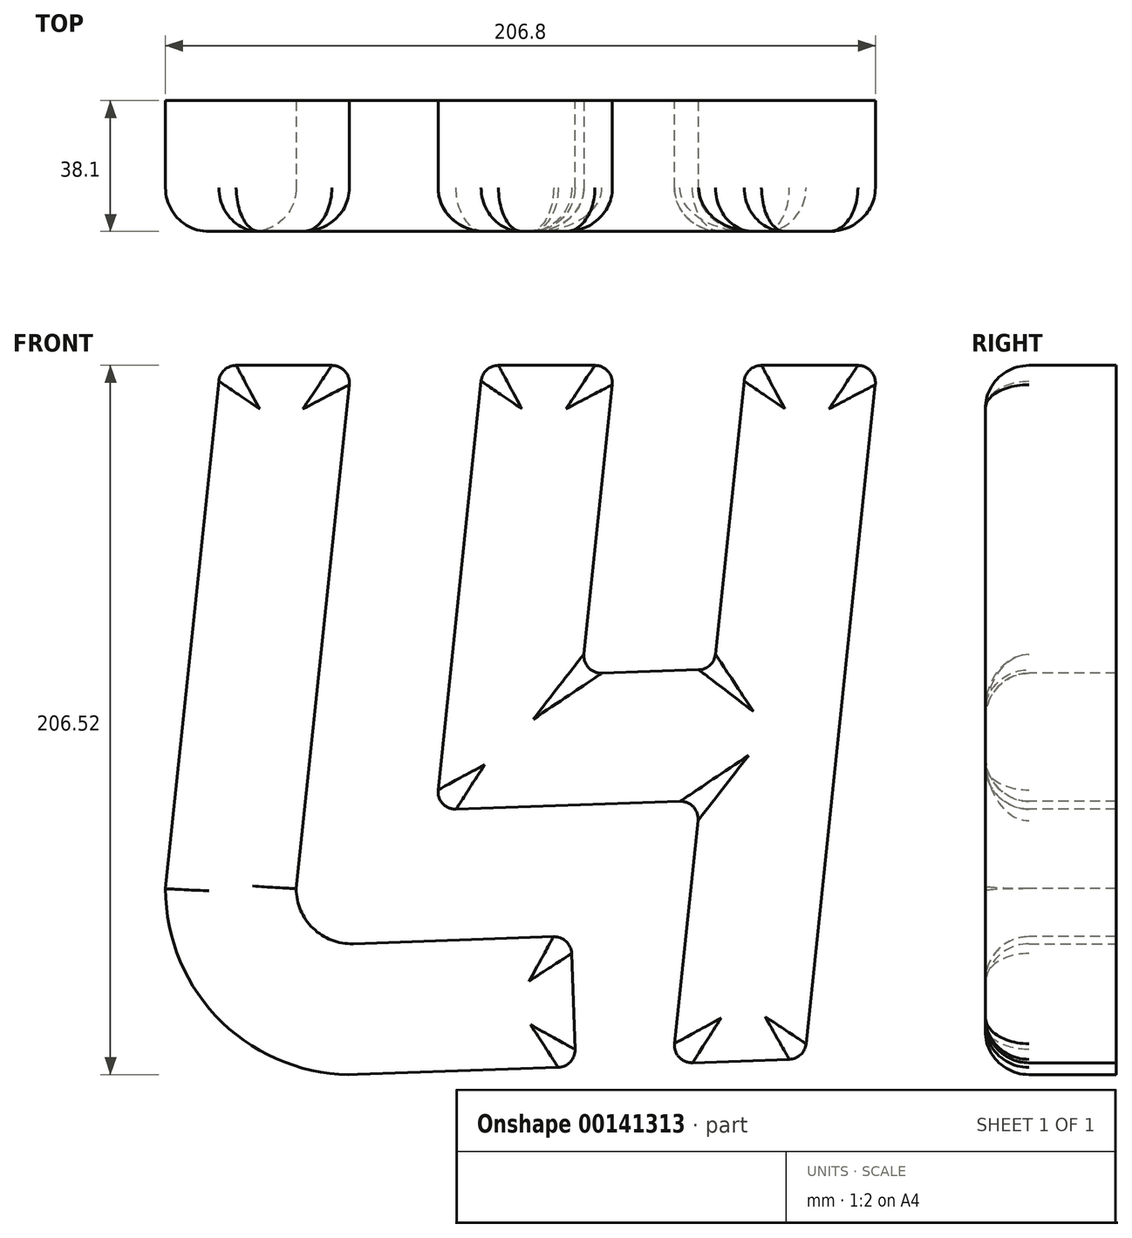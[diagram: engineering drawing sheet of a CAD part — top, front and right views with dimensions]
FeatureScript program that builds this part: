
annotation { "Feature Type Name" : "Feature", "Feature Type Description" : "" }
export const myFeature = defineFeature(function(context is Context, id is Id, definition is map)
    precondition{}
    {
        {
            var Q0;
            Q0=qCreatedBy(makeId("Top.planeOp"),FACE);
            cPlane(context, id + "F0", {"entities" : qUnion([Q0]), "cplaneType" : CPlaneType.OFFSET, "offset" : 76.2 * mm, "width" : 152.4 * mm, "height" : 152.4 * mm});
        }
        {
            var Q0;
            Q0=qCreatedBy(id+"F0.planeOp",FACE);
            var sketch = newSketch(context, id + "F1", { "sketchPlane" : qUnion([Q0])});
            skLineSegment(sketch, "E0.bottom", {"start": v(-19.05, 19.05) * mm, "end": v(19.05, 19.05) * mm});
            skLineSegment(sketch, "E0.top", {"start": v(-19.05, -19.05) * mm, "end": v(19.05, -19.05) * mm});
            skLineSegment(sketch, "E0.left", {"start": v(-19.05, 19.05) * mm, "end": v(-19.05, -19.05) * mm});
            skLineSegment(sketch, "E0.right", {"start": v(19.05, 19.05) * mm, "end": v(19.05, -19.05) * mm});
            skPoint(sketch, "E0.middle", {"position": v(0, 0) * mm});
            skSolve(sketch);
        }
        {
            var Q0;
            Q0=qCreatedBy(makeId("Front.planeOp"),FACE);
            var sketch = newSketch(context, id + "F2", { "sketchPlane" : qUnion([Q0])});
            skLineSegment(sketch, "E1", {"start": v(0, 0) * mm, "end": v(0, 76.2) * mm});
            skLineSegment(sketch, "E2", {"start": v(0, 0) * mm, "end": v(0, -76.2) * mm});
            skLineSegment(sketch, "E3", {"start": v(0, 76.2) * mm, "end": v(-16.02, -76.2) * mm});
            skSolve(sketch);
        }
        {
            var Q0;
            Q0=qCreatedBy(makeId("Top.planeOp"),FACE);
            cPlane(context, id + "F3", {"entities" : qUnion([Q0]), "cplaneType" : CPlaneType.OFFSET, "offset" : 76.2 * mm, "oppositeDirection" : true, "width" : 152.4 * mm, "height" : 152.4 * mm});
        }
        {
            var Q0;
            Q0=makeQuery(id+"F1.imprint","IMPRINT",FACE,{"disambiguationData":[TD([[makeQuery(id+"F1.imprint","IMPRINT",EDGE,{"derivedFrom":sQuery(id+"F1.wireOp",EDGE,"E0.bottom")}),-1.0]])]});
            var Q1;
            Q1=sQuery(id+"F2.wireOp",EDGE,"E3");
            sweep(context, id + "F4", {"profiles" : qUnion([Q0]), "path" : qUnion([Q1])});
        }
        {
            var Q0;
            Q0=qCreatedBy(id+"F3.planeOp",FACE);
            var sketch = newSketch(context, id + "F5", { "sketchPlane" : qUnion([Q0])});
            skLineSegment(sketch, "E4.0.0", {"start": v(3.03, -19.05) * mm, "end": v(3.03, 19.05) * mm});
            skLineSegment(sketch, "E4.0.1", {"start": v(3.03, 19.05) * mm, "end": v(19.05, 19.05) * mm});
            skLineSegment(sketch, "E4.0.2", {"start": v(19.05, 19.05) * mm, "end": v(19.05, -19.05) * mm});
            skLineSegment(sketch, "E4.0.3", {"start": v(19.05, -19.05) * mm, "end": v(3.03, -19.05) * mm});
            skSolve(sketch);
        }
        {
            var Q0;
            Q0=makeQuery(id+"F4.opSweep","CAP_FACE",FACE,{"disambiguationData":[OSD([sQuery(id+"F1.wireOp",EDGE,"E0.bottom"),sQuery(id+"F1.wireOp",EDGE,"E0.top"),sQuery(id+"F1.wireOp",EDGE,"E0.left"),sQuery(id+"F1.wireOp",EDGE,"E0.right"),sQuery(id+"F2.wireOp",VERTEX,"E3.end")])],"isStart":false});
            var Q1;
            Q1=sQuery(id+"F5.wireOp",EDGE,"E4.0.2");
            revolve(context, id + "F6", {"operationType" : NewBodyOperationType.ADD, "entities" : qUnion([Q0]), "axis" : qUnion([Q1]), "revolveType" : RevolveType.ONE_DIRECTION, "angle" : 92 * degree});
        }
        {
            var Q0;
            Q0=makeQuery(id+"F6.opRevolve","CAP_FACE",FACE,{"disambiguationData":[OSD([sQuery(id+"F1.wireOp",EDGE,"E0.bottom"),sQuery(id+"F1.wireOp",EDGE,"E0.top"),sQuery(id+"F1.wireOp",EDGE,"E0.left"),sQuery(id+"F1.wireOp",EDGE,"E0.right"),sQuery(id+"F2.wireOp",VERTEX,"E3.end")])],"isStart":false});
            extrude(context, id + "F7", {"entities" : qUnion([Q0]), "operationType" : NewBodyOperationType.ADD, "depth" : 63.5 * mm});
        }
        {
            var Q0;
            Q0=qCreatedBy(makeId("Front.planeOp"),FACE);
            cPlane(context, id + "F8", {"entities" : qUnion([Q0]), "cplaneType" : CPlaneType.OFFSET, "offset" : 19.05 * mm, "oppositeDirection" : true, "width" : 152.4 * mm, "height" : 152.4 * mm});
        }
        {
            var Q0;
            Q0=qCreatedBy(id+"F8.planeOp",FACE);
            var sketch = newSketch(context, id + "F9", { "sketchPlane" : qUnion([Q0])});
            skLineSegment(sketch, "E5.0.0", {"start": v(-19.05, 76.2) * mm, "end": v(-35.07, -76.2) * mm});
            skArc(sketch, "E5.0.1", {"start": v(-35.07, -76.2) * mm, "mid": v(-18.54, -115.13) * mm, "end": v(20.94, -130.28) * mm});
            skLineSegment(sketch, "E5.0.2", {"start": v(20.94, -130.28) * mm, "end": v(84.4, -128.07) * mm});
            skLineSegment(sketch, "E5.0.3", {"start": v(83.07, -90) * mm, "end": v(84.4, -128.07) * mm});
            skLineSegment(sketch, "E5.0.4", {"start": v(83.07, -90) * mm, "end": v(19.6, -92.2) * mm});
            skArc(sketch, "E5.0.5", {"start": v(19.6, -92.2) * mm, "mid": v(7.92, -87.72) * mm, "end": v(3.03, -76.2) * mm});
            skLineSegment(sketch, "E5.0.6", {"start": v(3.03, -76.2) * mm, "end": v(19.05, 76.2) * mm});
            skLineSegment(sketch, "E5.0.7", {"start": v(19.05, 76.2) * mm, "end": v(-19.05, 76.2) * mm});
            skLineSegment(sketch, "E6", {"start": v(14, 28.06) * mm, "end": v(51.88, 24.08) * mm, "construction": true});
            skLineSegment(sketch, "E7", {"start": v(72.28, -90.37) * mm, "end": v(70.95, -52.3) * mm, "construction": true});
            skLineSegment(sketch, "E8", {"start": v(51.88, 24.08) * mm, "end": v(57.36, 76.2) * mm});
            skLineSegment(sketch, "E9", {"start": v(51.88, 24.08) * mm, "end": v(43.75, -53.24) * mm});
            skLineSegment(sketch, "E10", {"start": v(43.75, -53.24) * mm, "end": v(120.66, -50.56) * mm});
            skLineSegment(sketch, "E11", {"start": v(50.4, 10.01) * mm, "end": v(88.3, 6.03) * mm, "construction": true});
            skLineSegment(sketch, "E12", {"start": v(88.3, 6.03) * mm, "end": v(95.67, 76.2) * mm});
            skLineSegment(sketch, "E13", {"start": v(57.36, 76.2) * mm, "end": v(95.67, 76.2) * mm});
            skLineSegment(sketch, "E14", {"start": v(113.89, -50.8) * mm, "end": v(112.56, -12.72) * mm, "construction": true});
            skLineSegment(sketch, "E15", {"start": v(112.56, -12.72) * mm, "end": v(86.23, -13.64) * mm});
            skLineSegment(sketch, "E16", {"start": v(88.3, 6.03) * mm, "end": v(86.23, -13.64) * mm});
            skLineSegment(sketch, "E17", {"start": v(90.92, 30.97) * mm, "end": v(128.8, 26.98) * mm, "construction": true});
            skLineSegment(sketch, "E18", {"start": v(128.8, 26.98) * mm, "end": v(133.98, 76.2) * mm});
            skLineSegment(sketch, "E19", {"start": v(112.56, -12.72) * mm, "end": v(124.68, -12.3) * mm});
            skLineSegment(sketch, "E20", {"start": v(128.8, 26.98) * mm, "end": v(124.68, -12.3) * mm});
            skLineSegment(sketch, "E21", {"start": v(126.2, 2.22) * mm, "end": v(164.1, -1.77) * mm, "construction": true});
            skLineSegment(sketch, "E22", {"start": v(164.1, -1.77) * mm, "end": v(172.29, 76.2) * mm});
            skLineSegment(sketch, "E23", {"start": v(133.98, 76.2) * mm, "end": v(172.29, 76.2) * mm});
            skLineSegment(sketch, "E24", {"start": v(164.1, -1.77) * mm, "end": v(151.06, -125.74) * mm});
            skLineSegment(sketch, "E25", {"start": v(125.38, -5.63) * mm, "end": v(124.68, -12.3) * mm});
            skLineSegment(sketch, "E26", {"start": v(112.61, -127.08) * mm, "end": v(151.06, -125.74) * mm});
            skLineSegment(sketch, "E27.trimOffspring", {"start": v(120.66, -50.56) * mm, "end": v(112.61, -127.08) * mm});
            skSolve(sketch);
        }
        {
            var Q0;
            Q0 = qSketchRegion(id + "F9", true);
            extrude(context, id + "F10", {"entities" : qUnion([Q0]), "operationType" : NewBodyOperationType.ADD, "depth" : 38.1 * mm});
        }
        {
            var Q0;
            Q0=makeQuery(id+"F4.opSweep","SWEPT_EDGE",EDGE,{"disambiguationData":[OSD([sQuery(id+"F1.wireOp",EDGE,"E0.top"),sQuery(id+"F1.wireOp",EDGE,"E0.left"),sQuery(id+"F2.wireOp",EDGE,"E3")])]});
            var Q1;
            Q1=makeQuery(id+"F6.opRevolve","SWEPT_EDGE",EDGE,{"disambiguationData":[OSD([sQuery(id+"F1.wireOp",EDGE,"E0.top"),sQuery(id+"F1.wireOp",EDGE,"E0.left"),sQuery(id+"F2.wireOp",EDGE,"E3")])]});
            var Q2;
            Q2=makeQuery(id+"F7.opExtrude","SWEPT_EDGE",EDGE,{"disambiguationData":[OSD([sQuery(id+"F1.wireOp",EDGE,"E0.top"),sQuery(id+"F1.wireOp",EDGE,"E0.right"),sQuery(id+"F2.wireOp",EDGE,"E3")])]});
            var Q3;
            Q3=makeQuery(id+"F6.opRevolve","SWEPT_EDGE",EDGE,{"disambiguationData":[OSD([sQuery(id+"F1.wireOp",EDGE,"E0.top"),sQuery(id+"F1.wireOp",EDGE,"E0.right"),sQuery(id+"F2.wireOp",EDGE,"E3")])]});
            var Q4;
            Q4=makeQuery(id+"F4.opSweep","SWEPT_EDGE",EDGE,{"disambiguationData":[OSD([sQuery(id+"F1.wireOp",EDGE,"E0.top"),sQuery(id+"F1.wireOp",EDGE,"E0.right"),sQuery(id+"F2.wireOp",EDGE,"E3")])]});
            var Q5;
            Q5=makeQuery(id+"F4.opSweep","CAP_EDGE",EDGE,{"disambiguationData":[OSD([sQuery(id+"F1.wireOp",EDGE,"E0.top"),sQuery(id+"F2.wireOp",VERTEX,"E3.start")])],"isStart":true});
            var Q6;
            Q6=makeQuery(id+"F7.opExtrude","CAP_EDGE",EDGE,{"disambiguationData":[OSD([sQuery(id+"F1.wireOp",EDGE,"E0.top"),sQuery(id+"F2.wireOp",VERTEX,"E3.end")])],"isStart":false});
            var Q7;
            Q7=makeQuery(id+"F10.opExtrude","CAP_EDGE",EDGE,{"disambiguationData":[OSD([sQuery(id+"F9.wireOp",EDGE,"E8"),sQuery(id+"F9.wireOp",EDGE,"E9")])],"isStart":false});
            var Q8;
            Q8=makeQuery(id+"F10.opExtrude","CAP_EDGE",EDGE,{"disambiguationData":[OSD([sQuery(id+"F9.wireOp",EDGE,"E13")])],"isStart":false});
            var Q9;
            Q9=makeQuery(id+"F10.opExtrude","CAP_EDGE",EDGE,{"disambiguationData":[OSD([sQuery(id+"F9.wireOp",EDGE,"E12"),sQuery(id+"F9.wireOp",EDGE,"E16")])],"isStart":false});
            var Q10;
            Q10=makeQuery(id+"F10.opExtrude","CAP_EDGE",EDGE,{"disambiguationData":[OSD([sQuery(id+"F9.wireOp",EDGE,"E15"),sQuery(id+"F9.wireOp",EDGE,"E19")])],"isStart":false});
            var Q11;
            Q11=makeQuery(id+"F10.opExtrude","CAP_EDGE",EDGE,{"disambiguationData":[OSD([sQuery(id+"F9.wireOp",EDGE,"E18"),sQuery(id+"F9.wireOp",EDGE,"E20"),sQuery(id+"F9.wireOp",EDGE,"E25")])],"isStart":false});
            var Q12;
            Q12=makeQuery(id+"F10.opExtrude","CAP_EDGE",EDGE,{"disambiguationData":[OSD([sQuery(id+"F9.wireOp",EDGE,"E23")])],"isStart":false});
            var Q13;
            Q13=makeQuery(id+"F10.opExtrude","CAP_EDGE",EDGE,{"disambiguationData":[OSD([sQuery(id+"F9.wireOp",EDGE,"E22"),sQuery(id+"F9.wireOp",EDGE,"E24")])],"isStart":false});
            var Q14;
            Q14=makeQuery(id+"F10.opExtrude","CAP_EDGE",EDGE,{"disambiguationData":[OSD([sQuery(id+"F9.wireOp",EDGE,"E26")])],"isStart":false});
            var Q15;
            Q15=makeQuery(id+"F10.opExtrude","CAP_EDGE",EDGE,{"disambiguationData":[OSD([sQuery(id+"F9.wireOp",EDGE,"E27.trimOffspring")])],"isStart":false});
            var Q16;
            Q16=makeQuery(id+"F10.opExtrude","CAP_EDGE",EDGE,{"disambiguationData":[OSD([sQuery(id+"F9.wireOp",EDGE,"E10")])],"isStart":false});
            fillet(context, id + "F11", {"entities" : qUnion([Q0, Q1, Q2, Q3, Q4, Q5, Q6, Q7, Q8, Q9, Q10, Q11, Q12, Q13, Q14, Q15, Q16]), "radius" : 12.7 * mm, "tangentPropagation" : true, "allowEdgeOverflow" : false});
        }
        {
            var Q0;
            Q0=makeQuery(id+"F4.opSweep","CAP_EDGE",EDGE,{"disambiguationData":[OSD([sQuery(id+"F1.wireOp",EDGE,"E0.left"),sQuery(id+"F2.wireOp",VERTEX,"E3.start")])],"isStart":true});
            var Q1;
            Q1=makeQuery(id+"F4.opSweep","CAP_EDGE",EDGE,{"disambiguationData":[OSD([sQuery(id+"F1.wireOp",EDGE,"E0.right"),sQuery(id+"F2.wireOp",VERTEX,"E3.start")])],"isStart":true});
            var Q2;
            Q2=makeQuery(id+"F7.opExtrude","CAP_EDGE",EDGE,{"disambiguationData":[OSD([sQuery(id+"F1.wireOp",EDGE,"E0.right"),sQuery(id+"F2.wireOp",VERTEX,"E3.end")])],"isStart":false});
            var Q3;
            Q3=makeQuery(id+"F7.opExtrude","CAP_EDGE",EDGE,{"disambiguationData":[OSD([sQuery(id+"F1.wireOp",EDGE,"E0.left"),sQuery(id+"F2.wireOp",VERTEX,"E3.end")])],"isStart":false});
            fillet(context, id + "F12", {"entities" : qUnion([Q0, Q1, Q2, Q3]), "radius" : 5.08 * mm, "tangentPropagation" : true, "allowEdgeOverflow" : false});
        }
        {
            var Q0;
            Q0=makeQuery(id+"F10.opExtrude","SWEPT_EDGE",EDGE,{"disambiguationData":[OSD([sQuery(id+"F9.wireOp",EDGE,"E8"),sQuery(id+"F9.wireOp",EDGE,"E13")])]});
            var Q1;
            Q1=makeQuery(id+"F10.opExtrude","SWEPT_EDGE",EDGE,{"disambiguationData":[OSD([sQuery(id+"F9.wireOp",EDGE,"E12"),sQuery(id+"F9.wireOp",EDGE,"E13")])]});
            var Q2;
            Q2=makeQuery(id+"F10.opExtrude","SWEPT_EDGE",EDGE,{"disambiguationData":[OSD([sQuery(id+"F9.wireOp",EDGE,"E9"),sQuery(id+"F9.wireOp",EDGE,"E10")])]});
            var Q3;
            Q3=makeQuery(id+"F10.opExtrude","SWEPT_EDGE",EDGE,{"disambiguationData":[OSD([sQuery(id+"F9.wireOp",EDGE,"E26"),sQuery(id+"F9.wireOp",EDGE,"E27.trimOffspring")])]});
            var Q4;
            Q4=makeQuery(id+"F10.opExtrude","SWEPT_EDGE",EDGE,{"disambiguationData":[OSD([sQuery(id+"F9.wireOp",EDGE,"E10"),sQuery(id+"F9.wireOp",EDGE,"E27.trimOffspring")])]});
            var Q5;
            Q5=makeQuery(id+"F10.opExtrude","SWEPT_EDGE",EDGE,{"disambiguationData":[OSD([sQuery(id+"F9.wireOp",EDGE,"E24"),sQuery(id+"F9.wireOp",EDGE,"E26")])]});
            var Q6;
            Q6=makeQuery(id+"F10.opExtrude","SWEPT_EDGE",EDGE,{"disambiguationData":[OSD([sQuery(id+"F9.wireOp",EDGE,"E22"),sQuery(id+"F9.wireOp",EDGE,"E23")])]});
            var Q7;
            Q7=makeQuery(id+"F10.opExtrude","SWEPT_EDGE",EDGE,{"disambiguationData":[OSD([sQuery(id+"F9.wireOp",EDGE,"E18"),sQuery(id+"F9.wireOp",EDGE,"E23")])]});
            fillet(context, id + "F13", {"entities" : qUnion([Q0, Q1, Q2, Q3, Q4, Q5, Q6, Q7]), "radius" : 5.08 * mm, "tangentPropagation" : true, "allowEdgeOverflow" : false});
        }
        {
            var Q0;
            Q0=makeQuery(id+"F10.opExtrude","SWEPT_EDGE",EDGE,{"disambiguationData":[OSD([sQuery(id+"F9.wireOp",EDGE,"E15"),sQuery(id+"F9.wireOp",EDGE,"E16")])]});
            var Q1;
            Q1=makeQuery(id+"F10.opExtrude","SWEPT_EDGE",EDGE,{"disambiguationData":[OSD([sQuery(id+"F9.wireOp",EDGE,"E19"),sQuery(id+"F9.wireOp",EDGE,"E25")])]});
            fillet(context, id + "F14", {"entities" : qUnion([Q0, Q1]), "radius" : 5.08 * mm, "tangentPropagation" : true, "allowEdgeOverflow" : false});
        }
    });
